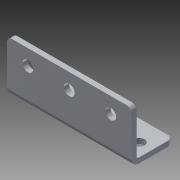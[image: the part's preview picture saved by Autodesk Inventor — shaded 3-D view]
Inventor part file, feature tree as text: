
AUTODESK INVENTOR PART (.ipt)
format: ipt  version: 2013 (Build 170138000, 138)  size: 172,032 bytes
history: native  units: in
note: dims shown in document units (in); Inventor stores cm internally (conversion verified against a paired STEP export)
features: sheet_metal_op x4, other x4, sketch x3, chamfer x1
ambient origin geometry x8: Origin, YZ Plane, XZ Plane, XY Plane, X Axis, Y Axis, Z Axis, Center Point
bodies: Solid1 (feature_tree)
feature tree (12):
  sheet_metal_op  "Face1"
  sheet_metal_op  "Flange1"
  chamfer  "Corner Round1"
  sketch  "Sketch1"  dims[d0=3.0in]
  other  "Plate1"
  sketch  "Sketch2"  dims[d1=1.0in]
  other  "Plate2"
  sheet_metal_op  "Bend1"
  sheet_metal_op  "Corner1"
  sketch  "Sketch3"  dims[d2=0.26in d3=2.375in d4=0.125in d5=0.125in d6=0.0625in d7=0.25in d8=0.125in d9=1.25in d10=90.0deg d11=0.05in d12=0.5in d13=0.125in d14=0.125in d15=2.0in d17=0.26in d19=0.875in d20=0.125in d21=0.0in d22=0.125in]
  other  "Cut1"
  other  "Definition1"
